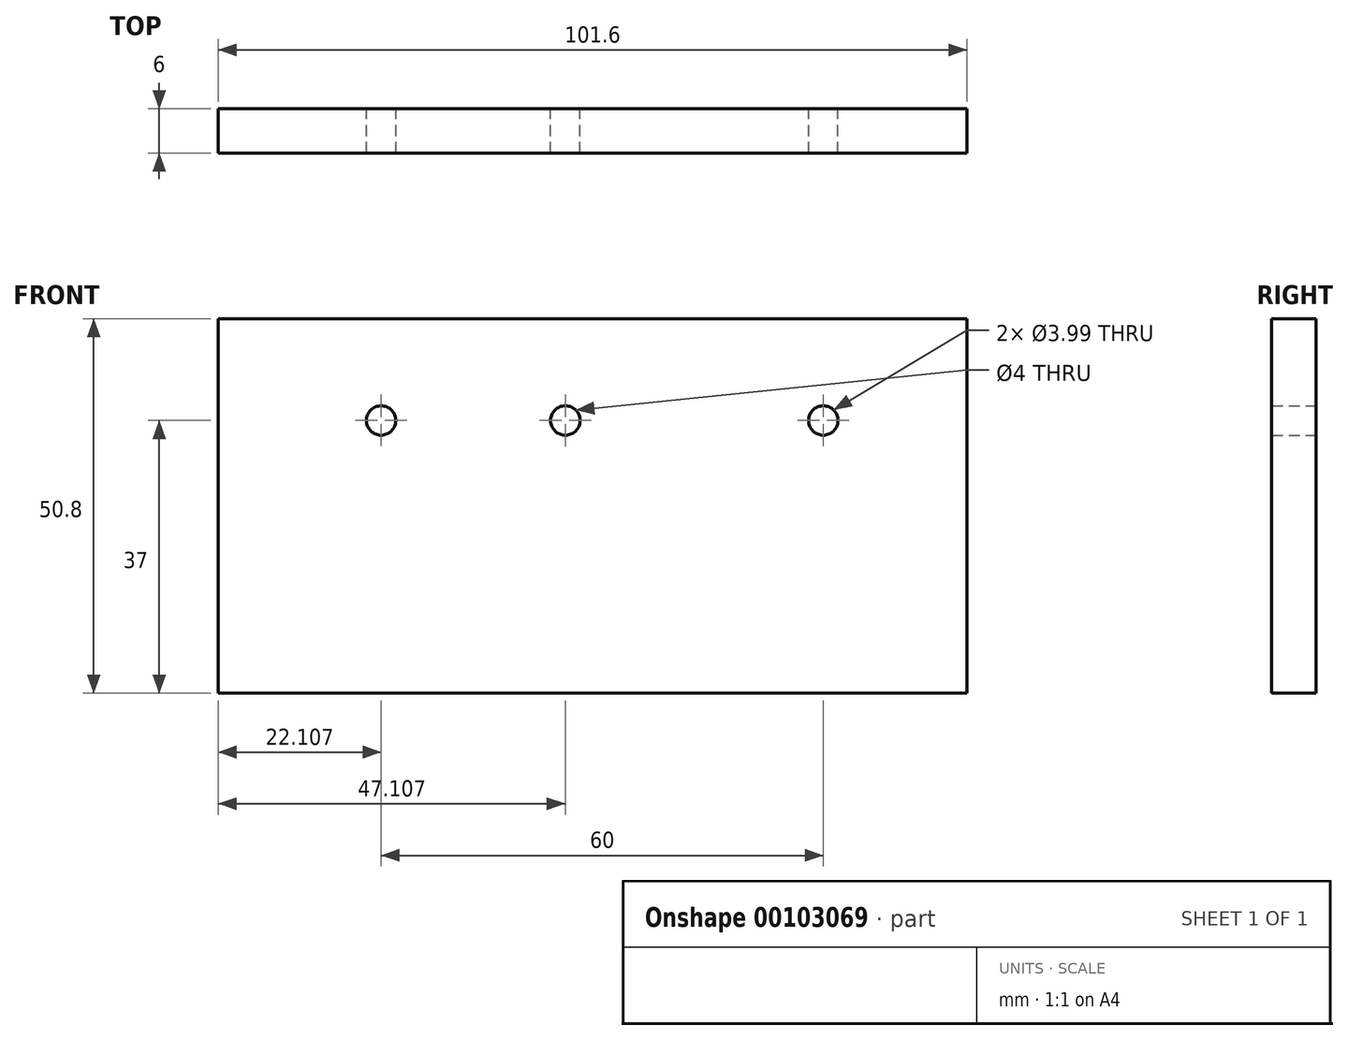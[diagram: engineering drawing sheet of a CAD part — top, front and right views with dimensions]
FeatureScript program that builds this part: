
annotation { "Feature Type Name" : "Feature", "Feature Type Description" : "" }
export const myFeature = defineFeature(function(context is Context, id is Id, definition is map)
    precondition{}
    {
        {
            var Q0;
            Q0=qCreatedBy(makeId("Front.planeOp"),FACE);
            var sketch = newSketch(context, id + "F0", { "sketchPlane" : qUnion([Q0])});
            skLineSegment(sketch, "E0.bottom", {"start": v(-108.68, 13.8) * mm, "end": v(-7.08, 13.8) * mm});
            skLineSegment(sketch, "E0.top", {"start": v(-108.68, -37) * mm, "end": v(-7.08, -37) * mm});
            skLineSegment(sketch, "E0.left", {"start": v(-108.68, 13.8) * mm, "end": v(-108.68, -37) * mm});
            skLineSegment(sketch, "E0.right", {"start": v(-7.08, 13.8) * mm, "end": v(-7.08, -37) * mm});
            skCircle(sketch, "E1", {"center": v(-61.57, 0) * mm, "radius": 2 * mm});
            skCircle(sketch, "E2", {"center": v(-86.57, 0) * mm, "radius": 2 * mm});
            skCircle(sketch, "E3", {"center": v(-26.57, 0) * mm, "radius": 2 * mm});
            skSolve(sketch);
        }
        {
            var Q0;
            Q0=makeQuery(id+"F0.imprint","IMPRINT",FACE,{"disambiguationData":[TD([[makeQuery(id+"F0.imprint","IMPRINT",EDGE,{"derivedFrom":sQuery(id+"F0.wireOp",EDGE,"E0.bottom")}),-1.0]])]});
            extrude(context, id + "F1", {"entities" : qUnion([Q0]), "depth" : 6 * mm});
        }
    });
